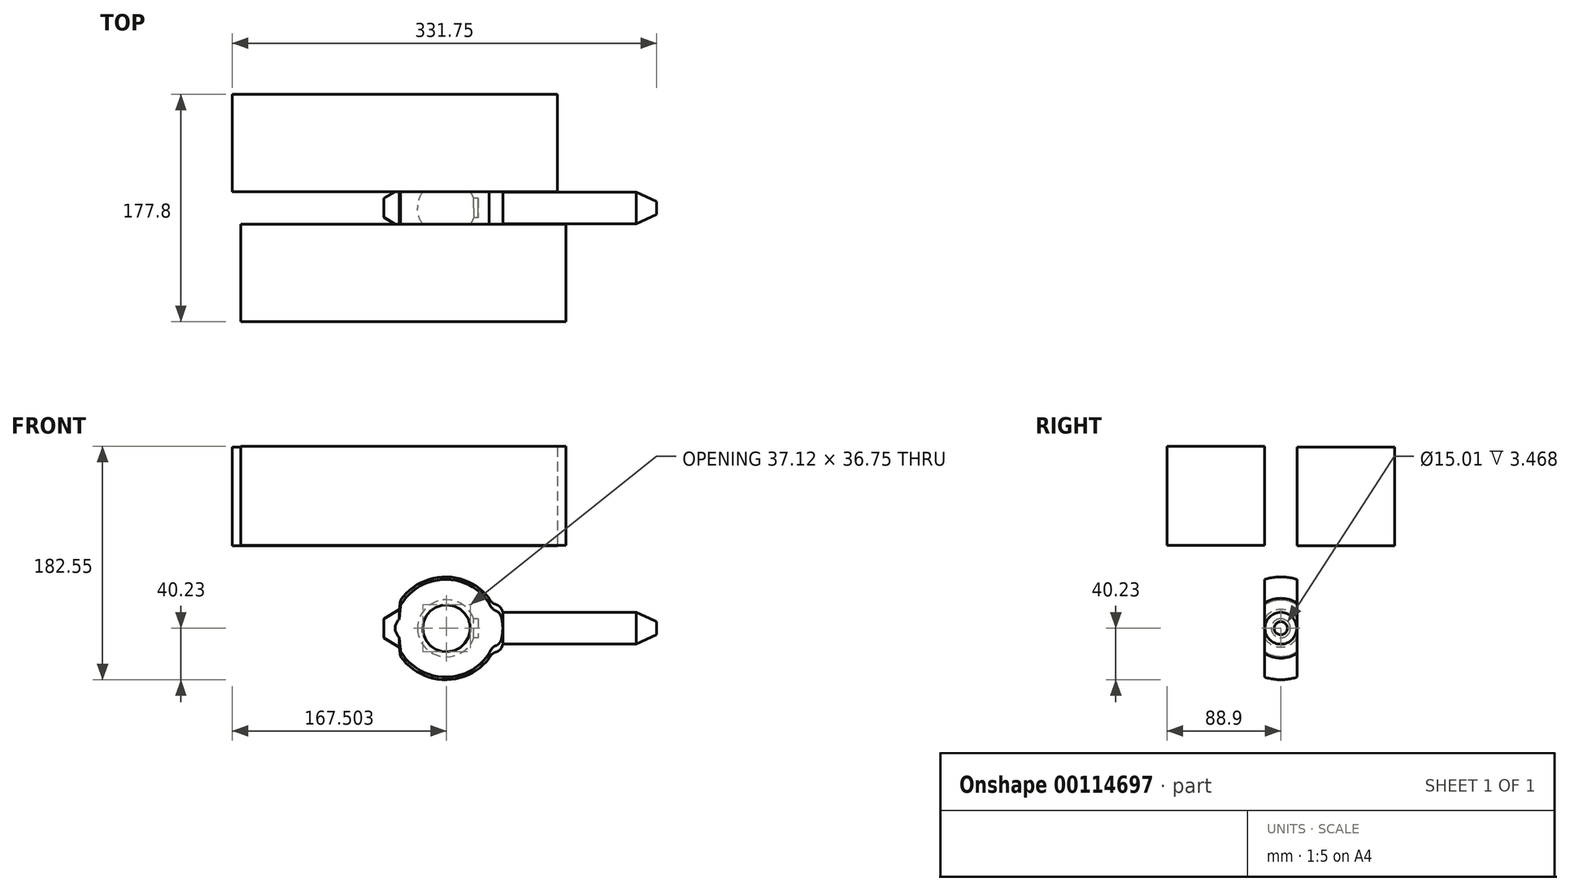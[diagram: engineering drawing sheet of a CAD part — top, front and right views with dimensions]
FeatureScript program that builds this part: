
annotation { "Feature Type Name" : "Feature", "Feature Type Description" : "" }
export const myFeature = defineFeature(function(context is Context, id is Id, definition is map)
    precondition{}
    {
        {
            var Q0;
            Q0=qCreatedBy(makeId("Front.planeOp"),FACE);
            var sketch = newSketch(context, id + "F0", { "sketchPlane" : qUnion([Q0])});
            skLineSegment(sketch, "E0", {"start": v(-422.64, -154.96) * mm, "end": v(282.56, -154.96) * mm});
            skLineSegment(sketch, "E1", {"start": v(76, -142.53) * mm, "end": v(180.17, -142.53) * mm});
            skLineSegment(sketch, "E2", {"start": v(180.17, -142.53) * mm, "end": v(196.18, -149.8) * mm});
            skLineSegment(sketch, "E3", {"start": v(196.18, -149.8) * mm, "end": v(196.18, -154.96) * mm});
            skLineSegment(sketch, "E4", {"start": v(200.2, 1.06) * mm, "end": v(-436.94, 1.06) * mm});
            skLineSegment(sketch, "E5", {"start": v(76, -142.53) * mm, "end": v(75.03, -140.17) * mm});
            skArc(sketch, "E6", {"start": v(65.19, -131.5) * mm, "mid": v(67.44, -134.64) * mm, "end": v(70.84, -136.48) * mm});
            skPoint(sketch, "E7.visualSharp", {"position": v(73.62, -136.77) * mm});
            skArc(sketch, "E7.filletArc", {"start": v(75.03, -140.17) * mm, "mid": v(73.36, -137.84) * mm, "end": v(70.84, -136.48) * mm});
            skArc(sketch, "E8", {"start": v(65.19, -131.5) * mm, "mid": v(30.3, -114.74) * mm, "end": v(-3.86, -132.92) * mm});
            skLineSegment(sketch, "E9", {"start": v(-3.86, -132.92) * mm, "end": v(-4.93, -140.25) * mm});
            skLineSegment(sketch, "E10", {"start": v(-4.93, -140.25) * mm, "end": v(-16.98, -147.51) * mm});
            skLineSegment(sketch, "E11", {"start": v(-16.98, -147.51) * mm, "end": v(-16.98, -154.96) * mm});
            skLineSegment(sketch, "E12.MirrorCS", {"start": v(-16.98, -162.4) * mm, "end": v(-16.98, -154.96) * mm});
            skLineSegment(sketch, "E13.MirrorCS", {"start": v(-4.93, -169.66) * mm, "end": v(-16.98, -162.4) * mm});
            skLineSegment(sketch, "E14.MirrorCS", {"start": v(-3.86, -177) * mm, "end": v(-4.93, -169.66) * mm});
            skArc(sketch, "E15.MirrorCS", {"start": v(65.19, -178.42) * mm, "mid": v(30.3, -195.18) * mm, "end": v(-3.86, -177) * mm});
            skArc(sketch, "E16.MirrorCS", {"start": v(65.19, -178.42) * mm, "mid": v(67.44, -175.28) * mm, "end": v(70.84, -173.44) * mm});
            skArc(sketch, "E17.MirrorCS", {"start": v(75.03, -169.75) * mm, "mid": v(73.36, -172.08) * mm, "end": v(70.84, -173.44) * mm});
            skLineSegment(sketch, "E18.MirrorCS", {"start": v(76, -167.39) * mm, "end": v(75.03, -169.75) * mm});
            skLineSegment(sketch, "E19", {"start": v(76, -167.39) * mm, "end": v(76, -142.53) * mm});
            skArc(sketch, "E20", {"start": v(53.22, -147.45) * mm, "mid": v(28.11, -132.95) * mm, "end": v(9.24, -154.96) * mm});
            skLineSegment(sketch, "E21", {"start": v(53.22, -147.45) * mm, "end": v(56.69, -147.45) * mm});
            skLineSegment(sketch, "E22", {"start": v(56.69, -147.45) * mm, "end": v(56.69, -154.96) * mm});
            skLineSegment(sketch, "E23.MirrorCS", {"start": v(53.22, -162.47) * mm, "end": v(56.69, -162.47) * mm});
            skLineSegment(sketch, "E24.MirrorCS", {"start": v(56.69, -162.47) * mm, "end": v(56.69, -154.96) * mm});
            skArc(sketch, "E25.MirrorCS", {"start": v(53.22, -162.47) * mm, "mid": v(28.11, -176.97) * mm, "end": v(9.24, -154.96) * mm});
            skSolve(sketch);
        }
        {
            var Q0;
            {var subQ1=sQuery(id+"F0.wireOp",EDGE,"E1");Q0=makeQuery(id+"F0.imprint","IMPRINT",FACE,{"disambiguationData":[TD([[makeQuery(id+"F0.imprint","IMPRINT",EDGE,{"derivedFrom":subQ1}),-1.0]])]});}
            var Q1;
            {var subQ3=sQuery(id+"F0.wireOp",EDGE,"E5");Q1=makeQuery(id+"F0.imprint","IMPRINT",FACE,{"disambiguationData":[TD([[makeQuery(id+"F0.imprint","IMPRINT",EDGE,{"derivedFrom":subQ3}),1.0]])]});}
            var Q2;
            Q2=sQuery(id+"F0.wireOp",EDGE,"E0");
            revolve(context, id + "F1", {"entities" : qUnion([Q0, Q1]), "axis" : qUnion([Q2]), "revolveType" : RevolveType.FULL});
        }
        {
            var Q0;
            Q0=qCreatedBy(makeId("Front.planeOp"),FACE);
            cPlane(context, id + "F2", {"entities" : qUnion([Q0]), "cplaneType" : CPlaneType.OFFSET, "offset" : 12.7 * mm, "width" : 152.4 * mm, "height" : 152.4 * mm});
        }
        {
            var Q0;
            Q0=qCreatedBy(id+"F2.planeOp",FACE);
            var sketch = newSketch(context, id + "F3", { "sketchPlane" : qUnion([Q0])});
            skLineSegment(sketch, "E26.bottom", {"start": v(-128.78, -90.2) * mm, "end": v(125.22, -90.2) * mm});
            skLineSegment(sketch, "E26.top", {"start": v(-128.78, -12.64) * mm, "end": v(125.22, -12.64) * mm});
            skLineSegment(sketch, "E26.left", {"start": v(-128.78, -90.2) * mm, "end": v(-128.78, -12.64) * mm});
            skLineSegment(sketch, "E26.right", {"start": v(125.22, -90.2) * mm, "end": v(125.22, -12.64) * mm});
            skSolve(sketch);
        }
        {
            var Q0;
            Q0=makeQuery(id+"F3.imprint","IMPRINT",FACE,{"disambiguationData":[TD([[makeQuery(id+"F3.imprint","IMPRINT",EDGE,{"derivedFrom":sQuery(id+"F3.wireOp",EDGE,"E26.bottom")}),1.0]])]});
            extrude(context, id + "F4", {"entities" : qUnion([Q0]), "depth" : 76.2 * mm});
        }
        {
            var Q0;
            Q0=makeQuery(id+"F4.opExtrude","SWEPT_FACE",FACE,{"disambiguationData":[OSD([sQuery(id+"F3.wireOp",EDGE,"E26.bottom")])]});
            extrude(context, id + "F5", {"entities" : qUnion([Q0]), "operationType" : NewBodyOperationType.REMOVE, "depth" : 508 * mm});
        }
        {
            var Q0;
            Q0=qCreatedBy(makeId("Front.planeOp"),FACE);
            cPlane(context, id + "F6", {"entities" : qUnion([Q0]), "cplaneType" : CPlaneType.OFFSET, "offset" : 12.7 * mm, "oppositeDirection" : true, "width" : 152.4 * mm, "height" : 152.4 * mm});
        }
        {
            var Q0;
            Q0=qCreatedBy(id+"F6.planeOp",FACE);
            var sketch = newSketch(context, id + "F7", { "sketchPlane" : qUnion([Q0])});
            skLineSegment(sketch, "E27.bottom", {"start": v(118.5, -13.28) * mm, "end": v(-135.57, -13.28) * mm});
            skLineSegment(sketch, "E27.top", {"start": v(118.5, -90.53) * mm, "end": v(-135.57, -90.53) * mm});
            skLineSegment(sketch, "E27.left", {"start": v(118.5, -13.28) * mm, "end": v(118.5, -90.53) * mm});
            skLineSegment(sketch, "E27.right", {"start": v(-135.57, -13.28) * mm, "end": v(-135.57, -90.53) * mm});
            skSolve(sketch);
        }
        {
            var Q0;
            Q0=makeQuery(id+"F7.imprint","IMPRINT",FACE,{"disambiguationData":[TD([[makeQuery(id+"F7.imprint","IMPRINT",EDGE,{"derivedFrom":sQuery(id+"F7.wireOp",EDGE,"E27.bottom")}),1.0]])]});
            extrude(context, id + "F8", {"entities" : qUnion([Q0]), "oppositeDirection" : true, "depth" : 76.2 * mm});
        }
        {
            var Q0;
            Q0=makeQuery(id+"F8.opExtrude","SWEPT_FACE",FACE,{"disambiguationData":[OSD([sQuery(id+"F7.wireOp",EDGE,"E27.top")])]});
            extrude(context, id + "F9", {"entities" : qUnion([Q0]), "operationType" : NewBodyOperationType.REMOVE, "depth" : 508 * mm});
        }
    });
